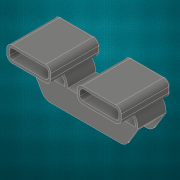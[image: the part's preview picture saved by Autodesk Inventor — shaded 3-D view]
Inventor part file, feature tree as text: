
AUTODESK INVENTOR PART (.ipt)
format: ipt  version: 2017 (Build 210142000, 142)  size: 310,272 bytes
history: native  units: in
note: dims shown in document units (in); Inventor stores cm internally (conversion verified against a paired STEP export)
features: extrude x4, sketch x4, fillet x3, shell x1
ambient origin geometry x8: Origin, YZ Plane, XZ Plane, XY Plane, X Axis, Y Axis, Z Axis, Center Point
bodies: Solid1 (feature_tree)
feature tree (12):
  extrude  "Extrusion1"  Depth=1.0in TaperAngle=0.0deg
  extrude  "Extrusion2"  Depth=0.0938in
  extrude  "Extrusion3"  Depth=1.25in
  extrude  "Extrusion4"  Depth=0.0938in TaperAngle=0.0deg
  fillet  "Fillet1"  Radius=0.625in
  fillet  "Fillet2"  Radius=0.625in
  fillet  "Fillet3"  Radius=2.5in
  shell  "Shell1"  Thickness=0.0625in
  sketch  "Sketch1"  dims[d1=0.75in d2=1.0in d3=0.0in]
  sketch  "Sketch2"  dims[d4=0.0938in d5=0.0938in]
  sketch  "Sketch3"  dims[d6=1.25in d7=1.25in]
  sketch  "Sketch4"  dims[d8=0.625in d9=1.0in d10=0.0in d11=0.625in d12=0.625in d13=2.5in d14=0.0625in d15=0.0625in d16=0.0625in d17=1.0in d18=0.0in d19=1.5625in d20=0.5625in d21=1.25in d22=0.5in d23=0.0in d24=0.0in d25=0.1875in d26=0.0625in d27=0.0938in d28=0.0938in]
